# Revit family: 94752104RVM001A
name_source: partatom
category: Equipamento especial
units: mm (PartAtom-declared; Revit-internal decimal feet)

## family parameters
Com base no plano de trabalho = Não
Compartilhado = Não
Corte com vazios quando carregada = Não
Cota do conector redondo = Utilizar diâmetro
Ponto de cálculo do ambiente = Não
Sempre na vertical = Sim
Tipo de parte = Normal

## types (1)
- Tramontina - Penta Plus 5GX Tri
    Classe de Construção = Classe 2
    Código de montagem = 94752/104
    Descrição = Tramontina Cooktop a Gás
    Desenvolvedor = Factory Cursos & Desenvolvimento
    Elevação padrão = 0 mm  [stored 0 ft]
    Fabricante = Tramontina
    Frequência = 50 - 60 Hz
    Modelo = Tramontina - Dominó 2ER 30
    Peso Bruto = 13,8 kg
    Peso liquido = 11,7 kg
    Potência Máx Rápido (1X) = 3,00 kW
    Potência Máx Semirrápido (2X) = 1,75 kW
    Potência Máx Tripla chama (1X) = 4,10 kW
    Potência Máx. Auxiliar (1X) = 1,00 kW
    Potência elétrica = 5 kW
    Potência térmica = 11,60 kW
    Rendimento Médio = 63%
    Site do desenvolvedor = www.factorycursos.com.br
    Tensão = 127 -  220 V
    Tipo de imagem = <Nenhum>
    URL = www.tramontina.com.br

note: [stored X ft] marks values corroborated as IEEE doubles in the binary element streams (Revit-internal decimal feet)
